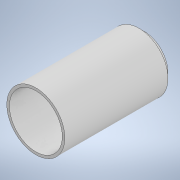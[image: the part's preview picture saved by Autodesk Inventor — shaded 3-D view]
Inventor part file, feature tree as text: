
AUTODESK INVENTOR PART (.ipt)
format: ipt  version: 2021 (Build 250183000, 183)  size: 321,536 bytes
history: native  units: in
note: dims shown in document units (in); Inventor stores cm internally (conversion verified against a paired STEP export)
features: extrude x3, sketch x3, fillet x1, chamfer x1, projected_geometry x1
ambient origin geometry x8: Origin, YZ Plane, XZ Plane, XY Plane, X Axis, Y Axis, Z Axis, Center Point
bodies: Solid1 (feature_tree)
feature tree (9):
  extrude  "Extrusion1"  Depth=3.2677in TaperAngle=0.0deg
  extrude  "Extrusion7"  Depth=3.2559in TaperAngle=0.0deg
  fillet  "Fillet12"  Radius=0.6693in
  extrude  "Extrusion15"  Depth=0.185in
  chamfer  "Chamfer9"  [1 undecoded]
  sketch  "Sketch2"  dims[d2=1.752in d3=3.2677in d4=0.0in]
  sketch  "Sketch9"  dims[d54=1.5945in d55=3.2559in d56=0.0in d117=0.6693in]
  projected_geometry  "Projected Loop7"
  sketch  "Sketch18"  dims[d122=0.122in d123=0.185in d124=0.0in d125=0.0in d130=0.1575in d131=0.0787in d132=45.0deg d19=0.0197in d20=0.0344in d21=0.0197in d22=0.0344in]
note: 1 required parameter value undecoded (feature->parameter linkage not recoverable at this tier; creation-order binding heuristic only, values carry confidence <= 0.55)
